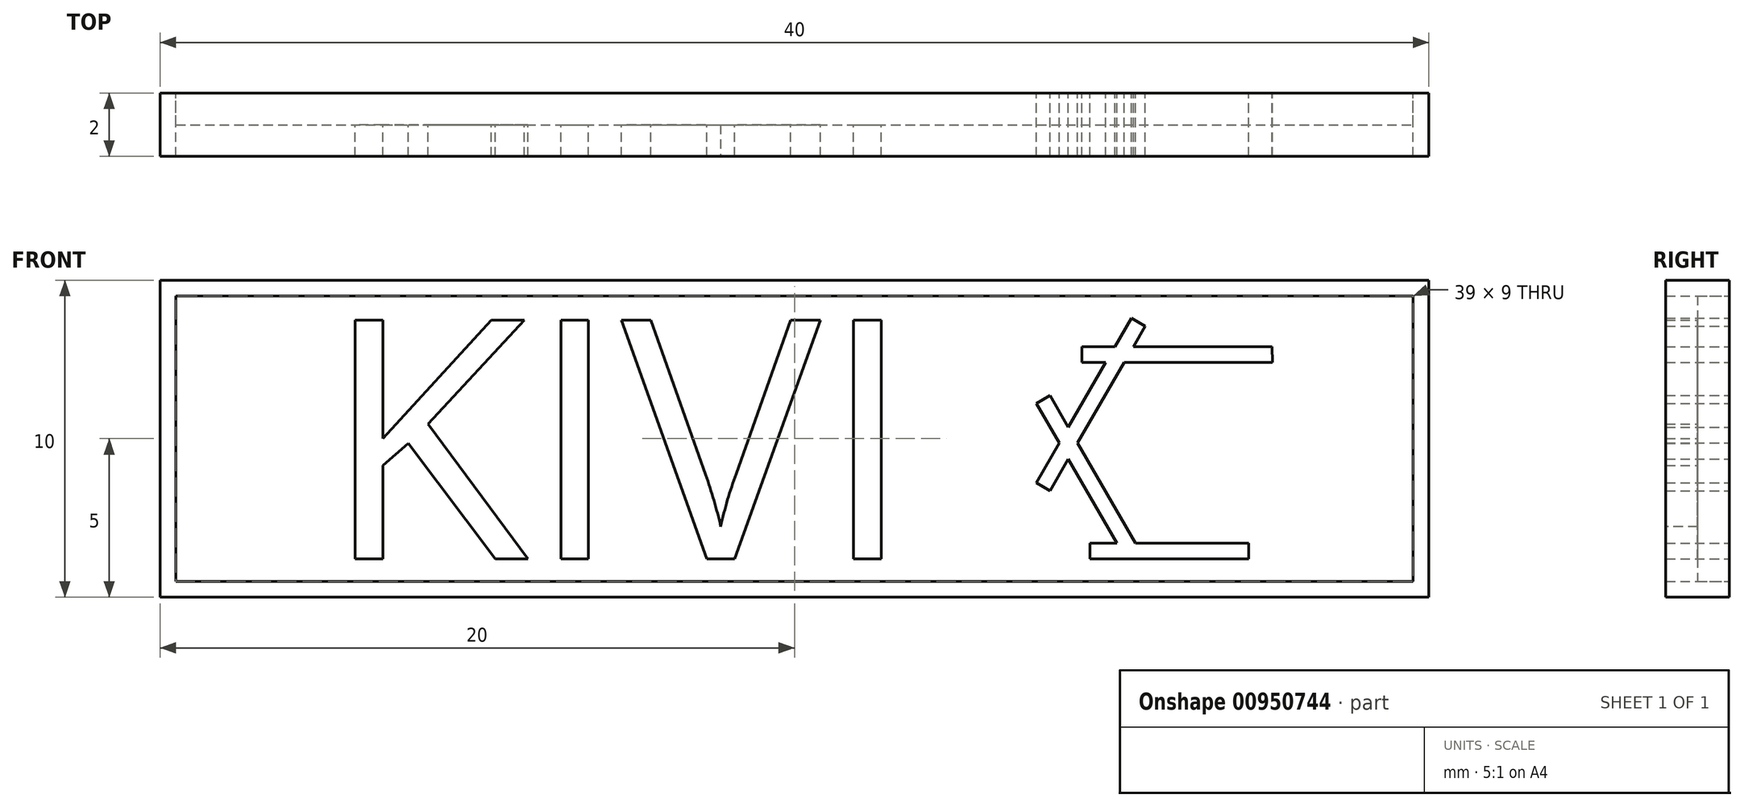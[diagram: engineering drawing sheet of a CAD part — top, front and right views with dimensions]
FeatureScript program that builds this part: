
annotation { "Feature Type Name" : "Feature", "Feature Type Description" : "" }
export const myFeature = defineFeature(function(context is Context, id is Id, definition is map)
    precondition{}
    {
        {
            var Q0;
            Q0=qCreatedBy(makeId("Front.planeOp"),FACE);
            var sketch = newSketch(context, id + "F0", { "sketchPlane" : qUnion([Q0])});
            skLineSegment(sketch, "E0.bottom", {"start": v(-20, 5) * mm, "end": v(20, 5) * mm});
            skLineSegment(sketch, "E0.top", {"start": v(-20, -5) * mm, "end": v(20, -5) * mm});
            skLineSegment(sketch, "E0.left", {"start": v(-20, 5) * mm, "end": v(-20, -5) * mm});
            skLineSegment(sketch, "E0.right", {"start": v(20, 5) * mm, "end": v(20, -5) * mm});
            skPoint(sketch, "E0.middle", {"position": v(0, 0) * mm});
            skLineSegment(sketch, "E1.top", {"start": v(-20, 4.5) * mm, "end": v(20, 4.5) * mm});
            skLineSegment(sketch, "E1.left", {"start": v(-20, 5) * mm, "end": v(-20, 4.5) * mm});
            skLineSegment(sketch, "E1.right", {"start": v(20, 5) * mm, "end": v(20, 4.5) * mm});
            skLineSegment(sketch, "E2.bottom", {"start": v(-20, 4.5) * mm, "end": v(-19.5, 4.5) * mm});
            skLineSegment(sketch, "E2.top", {"start": v(-20, -5) * mm, "end": v(-19.5, -5) * mm});
            skLineSegment(sketch, "E2.left", {"start": v(-20, 4.5) * mm, "end": v(-20, -5) * mm});
            skLineSegment(sketch, "E2.right", {"start": v(-19.5, 4.5) * mm, "end": v(-19.5, -5) * mm});
            skLineSegment(sketch, "E3.top", {"start": v(-20, -4.5) * mm, "end": v(20, -4.5) * mm});
            skLineSegment(sketch, "E3.left", {"start": v(-20, -5) * mm, "end": v(-20, -4.5) * mm});
            skLineSegment(sketch, "E3.right", {"start": v(20, -5) * mm, "end": v(20, -4.5) * mm});
            skLineSegment(sketch, "E4.bottom", {"start": v(20, -5) * mm, "end": v(19.5, -5) * mm});
            skLineSegment(sketch, "E4.top", {"start": v(20, 5) * mm, "end": v(19.5, 5) * mm});
            skLineSegment(sketch, "E4.left", {"start": v(20, -5) * mm, "end": v(20, 5) * mm});
            skLineSegment(sketch, "E4.right", {"start": v(19.5, -5) * mm, "end": v(19.5, 5) * mm});
            skSolve(sketch);
        }
        {
            var Q0;
            {var subQ0=sQuery(id+"F0.wireOp",EDGE,"E2.right");var subQ1=sQuery(id+"F0.wireOp",EDGE,"E1.top");var subQ2=makeQuery(id+"F0.imprint","INTERSECT",VERTEX,{"derivedFrom":[subQ1,subQ0]});Q0=makeQuery(id+"F0.imprint","IMPRINT",FACE,{"disambiguationData":[TD([[makeQuery(id+"F0.imprint","IMPRINT",EDGE,{"disambiguationData":[TD([[subQ2,-1.0]])],"derivedFrom":subQ1}),-1.0]])]});}
            var sketch = newSketch(context, id + "F1", { "sketchPlane" : qUnion([Q0])});
            skText(sketch, "E5", { "text": "KIVI", "fontName": "OpenSans-Regular.ttf"});
            const initialGuessF1  = {"E5": [-0.01488, -0.0038, 1, 0, 0.0076]};
            skSetInitialGuess(sketch, initialGuessF1);
            skSolve(sketch);
        }
        {
            var Q0;
            {var subQ0=sQuery(id+"F0.wireOp",EDGE,"E2.right");var subQ1=sQuery(id+"F0.wireOp",EDGE,"E1.top");var subQ2=makeQuery(id+"F0.imprint","INTERSECT",VERTEX,{"derivedFrom":[subQ1,subQ0]});Q0=makeQuery(id+"F0.imprint","IMPRINT",FACE,{"disambiguationData":[TD([[makeQuery(id+"F0.imprint","IMPRINT",EDGE,{"disambiguationData":[TD([[subQ2,-1.0]])],"derivedFrom":subQ1}),-1.0]])]});}
            var Q1;
            {var subQ0=sQuery(id+"F0.wireOp",EDGE,"E2.right");var subQ1=sQuery(id+"F0.wireOp",EDGE,"E1.top");var subQ2=makeQuery(id+"F0.imprint","INTERSECT",VERTEX,{"derivedFrom":[subQ1,subQ0]});Q1=makeQuery(id+"F0.imprint","IMPRINT",FACE,{"disambiguationData":[TD([[makeQuery(id+"F0.imprint","IMPRINT",EDGE,{"disambiguationData":[TD([[subQ2,-1.0]])],"derivedFrom":subQ1}),-1.0]])]});}
            var Q2;
            {var subQ0=sQuery(id+"F0.wireOp",EDGE,"E2.right");var subQ1=sQuery(id+"F0.wireOp",EDGE,"E1.top");var subQ2=makeQuery(id+"F0.imprint","INTERSECT",VERTEX,{"derivedFrom":[subQ1,subQ0]});Q2=makeQuery(id+"F0.imprint","IMPRINT",FACE,{"disambiguationData":[TD([[makeQuery(id+"F0.imprint","IMPRINT",EDGE,{"disambiguationData":[TD([[subQ2,-1.0]])],"derivedFrom":subQ1}),-1.0]])]});}
            var Q3;
            {var subQ0=sQuery(id+"F0.wireOp",EDGE,"E2.right");var subQ1=sQuery(id+"F0.wireOp",EDGE,"E1.top");var subQ2=makeQuery(id+"F0.imprint","INTERSECT",VERTEX,{"derivedFrom":[subQ1,subQ0]});Q3=makeQuery(id+"F0.imprint","IMPRINT",FACE,{"disambiguationData":[TD([[makeQuery(id+"F0.imprint","IMPRINT",EDGE,{"disambiguationData":[TD([[subQ2,-1.0]])],"derivedFrom":subQ1}),-1.0]])]});}
            var Q4;
            {var subQ0=sQuery(id+"F0.wireOp",EDGE,"E2.right");var subQ1=sQuery(id+"F0.wireOp",EDGE,"E1.top");var subQ2=makeQuery(id+"F0.imprint","INTERSECT",VERTEX,{"derivedFrom":[subQ1,subQ0]});Q4=makeQuery(id+"F0.imprint","IMPRINT",FACE,{"disambiguationData":[TD([[makeQuery(id+"F0.imprint","IMPRINT",EDGE,{"disambiguationData":[TD([[subQ2,-1.0]])],"derivedFrom":subQ1}),-1.0]])]});}
            var sketch = newSketch(context, id + "F2", { "sketchPlane" : qUnion([Q0, Q1, Q2, Q3, Q4])});
            skLineSegment(sketch, "E6.bottom", {"start": v(9.06, 2.4) * mm, "end": v(15.06, 2.4) * mm});
            skLineSegment(sketch, "E6.left", {"start": v(9.06, 2.4) * mm, "end": v(9.06, 2.9) * mm});
            skLineSegment(sketch, "E6.right", {"start": v(15.06, 2.4) * mm, "end": v(15.06, 2.9) * mm});
            skPoint(sketch, "E6.middle", {"position": v(12.06, 2.65) * mm});
            skPoint(sketch, "E7.middle", {"position": v(11.48, -0.59) * mm});
            skLineSegment(sketch, "E8.bottom", {"start": v(14.32, -3.8) * mm, "end": v(9.32, -3.8) * mm});
            skLineSegment(sketch, "E8.left", {"start": v(14.32, -3.8) * mm, "end": v(14.32, -3.3) * mm});
            skLineSegment(sketch, "E8.right", {"start": v(9.32, -3.8) * mm, "end": v(9.32, -3.3) * mm});
            skPoint(sketch, "E8.middle", {"position": v(11.82, -3.55) * mm});
            skLineSegment(sketch, "E9.bottom", {"start": v(8.06, -1.65) * mm, "end": v(7.62, -1.4) * mm});
            skLineSegment(sketch, "E9.top", {"start": v(11.06, 3.55) * mm, "end": v(10.62, 3.8) * mm});
            skLineSegment(sketch, "E9.left", {"start": v(8.06, -1.65) * mm, "end": v(11.06, 3.55) * mm});
            skLineSegment(sketch, "E9.right", {"start": v(7.62, -1.4) * mm, "end": v(10.62, 3.8) * mm});
            skPoint(sketch, "E9.middle", {"position": v(10.33, 1.27) * mm});
            skLineSegment(sketch, "E10.bottom", {"start": v(10.8, -3.4) * mm, "end": v(10.37, -3.65) * mm});
            skLineSegment(sketch, "E10.top", {"start": v(8.06, 1.36) * mm, "end": v(7.62, 1.11) * mm});
            skLineSegment(sketch, "E10.left", {"start": v(10.8, -3.4) * mm, "end": v(8.06, 1.36) * mm});
            skLineSegment(sketch, "E10.right", {"start": v(10.37, -3.65) * mm, "end": v(7.62, 1.11) * mm});
            skPoint(sketch, "E10.middle", {"position": v(13.45, 1.64) * mm});
            skLineSegment(sketch, "E11", {"start": v(9.32, -3.3) * mm, "end": v(14.32, -3.3) * mm});
            skLineSegment(sketch, "E12", {"start": v(9.06, 2.9) * mm, "end": v(15.06, 2.9) * mm});
            skSolve(sketch);
        }
        {
            var Q0;
            Q0 = qSketchRegion(id + "F2", true);
            var Q1;
            {var subQ1=sQuery(id+"F0.wireOp",EDGE,"E0.left");var subQ6=sQuery(id+"F0.wireOp",EDGE,"E0.bottom");var subQ7=makeQuery(id+"F0.imprint","INTERSECT",VERTEX,{"derivedFrom":[subQ6,subQ1]});Q1=makeQuery(id+"F0.imprint","IMPRINT",FACE,{"disambiguationData":[TD([[makeQuery(id+"F0.imprint","IMPRINT",EDGE,{"disambiguationData":[TD([[subQ7,-1.0]])],"derivedFrom":subQ6}),-1.0]])]});}
            var Q2;
            {var subQ0=sQuery(id+"F0.wireOp",EDGE,"E1.top");var subQ1=sQuery(id+"F0.wireOp",EDGE,"E0.left");var subQ2=makeQuery(id+"F0.imprint","INTERSECT",VERTEX,{"derivedFrom":[subQ1,subQ0]});Q2=makeQuery(id+"F0.imprint","IMPRINT",FACE,{"disambiguationData":[TD([[makeQuery(id+"F0.imprint","IMPRINT",EDGE,{"disambiguationData":[TD([[subQ2,-1.0]])],"derivedFrom":subQ1}),1.0]])]});}
            var Q3;
            {var subQ0=sQuery(id+"F0.wireOp",EDGE,"E2.right");var subQ1=sQuery(id+"F0.wireOp",EDGE,"E0.top");var subQ2=makeQuery(id+"F0.imprint","INTERSECT",VERTEX,{"derivedFrom":[subQ1,subQ0]});Q3=makeQuery(id+"F0.imprint","IMPRINT",FACE,{"disambiguationData":[TD([[makeQuery(id+"F0.imprint","IMPRINT",EDGE,{"disambiguationData":[TD([[subQ2,-1.0]])],"derivedFrom":subQ1}),1.0]])]});}
            var Q4;
            {var subQ0=sQuery(id+"F0.wireOp",EDGE,"E2.right");var subQ1=sQuery(id+"F0.wireOp",EDGE,"E0.top");var subQ2=makeQuery(id+"F0.imprint","INTERSECT",VERTEX,{"derivedFrom":[subQ1,subQ0]});Q4=makeQuery(id+"F0.imprint","IMPRINT",FACE,{"disambiguationData":[TD([[makeQuery(id+"F0.imprint","IMPRINT",EDGE,{"disambiguationData":[TD([[subQ2,1.0]])],"derivedFrom":subQ1}),1.0]])]});}
            var Q5;
            {var subQ0=sQuery(id+"F0.wireOp",EDGE,"E0.right");var subQ1=sQuery(id+"F0.wireOp",EDGE,"E0.top");var subQ2=makeQuery(id+"F0.imprint","INTERSECT",VERTEX,{"derivedFrom":[subQ1,subQ0]});Q5=makeQuery(id+"F0.imprint","IMPRINT",FACE,{"disambiguationData":[TD([[makeQuery(id+"F0.imprint","IMPRINT",EDGE,{"disambiguationData":[TD([[subQ2,1.0]])],"derivedFrom":subQ1}),1.0]])]});}
            var Q6;
            {var subQ0=sQuery(id+"F0.wireOp",EDGE,"E1.top");var subQ1=sQuery(id+"F0.wireOp",EDGE,"E0.right");var subQ2=makeQuery(id+"F0.imprint","INTERSECT",VERTEX,{"derivedFrom":[subQ1,subQ0]});Q6=makeQuery(id+"F0.imprint","IMPRINT",FACE,{"disambiguationData":[TD([[makeQuery(id+"F0.imprint","IMPRINT",EDGE,{"disambiguationData":[TD([[subQ2,-1.0]])],"derivedFrom":subQ1}),-1.0]])]});}
            var Q7;
            {var subQ0=sQuery(id+"F0.wireOp",EDGE,"E0.right");var subQ1=sQuery(id+"F0.wireOp",EDGE,"E0.bottom");var subQ2=makeQuery(id+"F0.imprint","INTERSECT",VERTEX,{"derivedFrom":[subQ1,subQ0]});Q7=makeQuery(id+"F0.imprint","IMPRINT",FACE,{"disambiguationData":[TD([[makeQuery(id+"F0.imprint","IMPRINT",EDGE,{"disambiguationData":[TD([[subQ2,1.0]])],"derivedFrom":subQ1}),-1.0]])]});}
            extrude(context, id + "F3", {"entities" : qUnion([Q0, Q1, Q2, Q3, Q4, Q5, Q6, Q7]), "depth" : 2 * mm, "offsetDistance" : 25 * mm});
        }
        {
            var Q0;
            Q0 = qSketchRegion(id + "F1", true);
            extrude(context, id + "F4", {"entities" : qUnion([Q0]), "depth" : 2 * mm, "offsetDistance" : 25 * mm});
        }
        {
            var Q0;
            Q0=makeQuery(id+"F0.imprint","IMPRINT",FACE,{"disambiguationData":[TD([[makeQuery(id+"F0.imprint","IMPRINT",EDGE,{"derivedFrom":sQuery(id+"F0.wireOp",EDGE,"C3bEAGVS-fK24-FECI-0hbw-yxprCsJxxsqK")}),-1.0]])]});
            var Q1;
            {var subQ0=sQuery(id+"F0.wireOp",EDGE,"E2.right");var subQ1=sQuery(id+"F0.wireOp",EDGE,"E1.top");var subQ2=makeQuery(id+"F0.imprint","INTERSECT",VERTEX,{"derivedFrom":[subQ1,subQ0]});Q1=makeQuery(id+"F0.imprint","IMPRINT",FACE,{"disambiguationData":[TD([[makeQuery(id+"F0.imprint","IMPRINT",EDGE,{"disambiguationData":[TD([[subQ2,-1.0]])],"derivedFrom":subQ1}),-1.0]])]});}
            extrude(context, id + "F5", {"entities" : qUnion([Q0, Q1]), "depth" : 1 * mm, "offsetDistance" : 25 * mm});
        }
        {
            var Q0;
            Q0 = qSketchRegion(id + "F1", true);
            extrude(context, id + "F6", {"entities" : qUnion([Q0]), "operationType" : NewBodyOperationType.ADD, "depth" : 2 * mm, "offsetDistance" : 25 * mm});
        }
    });
